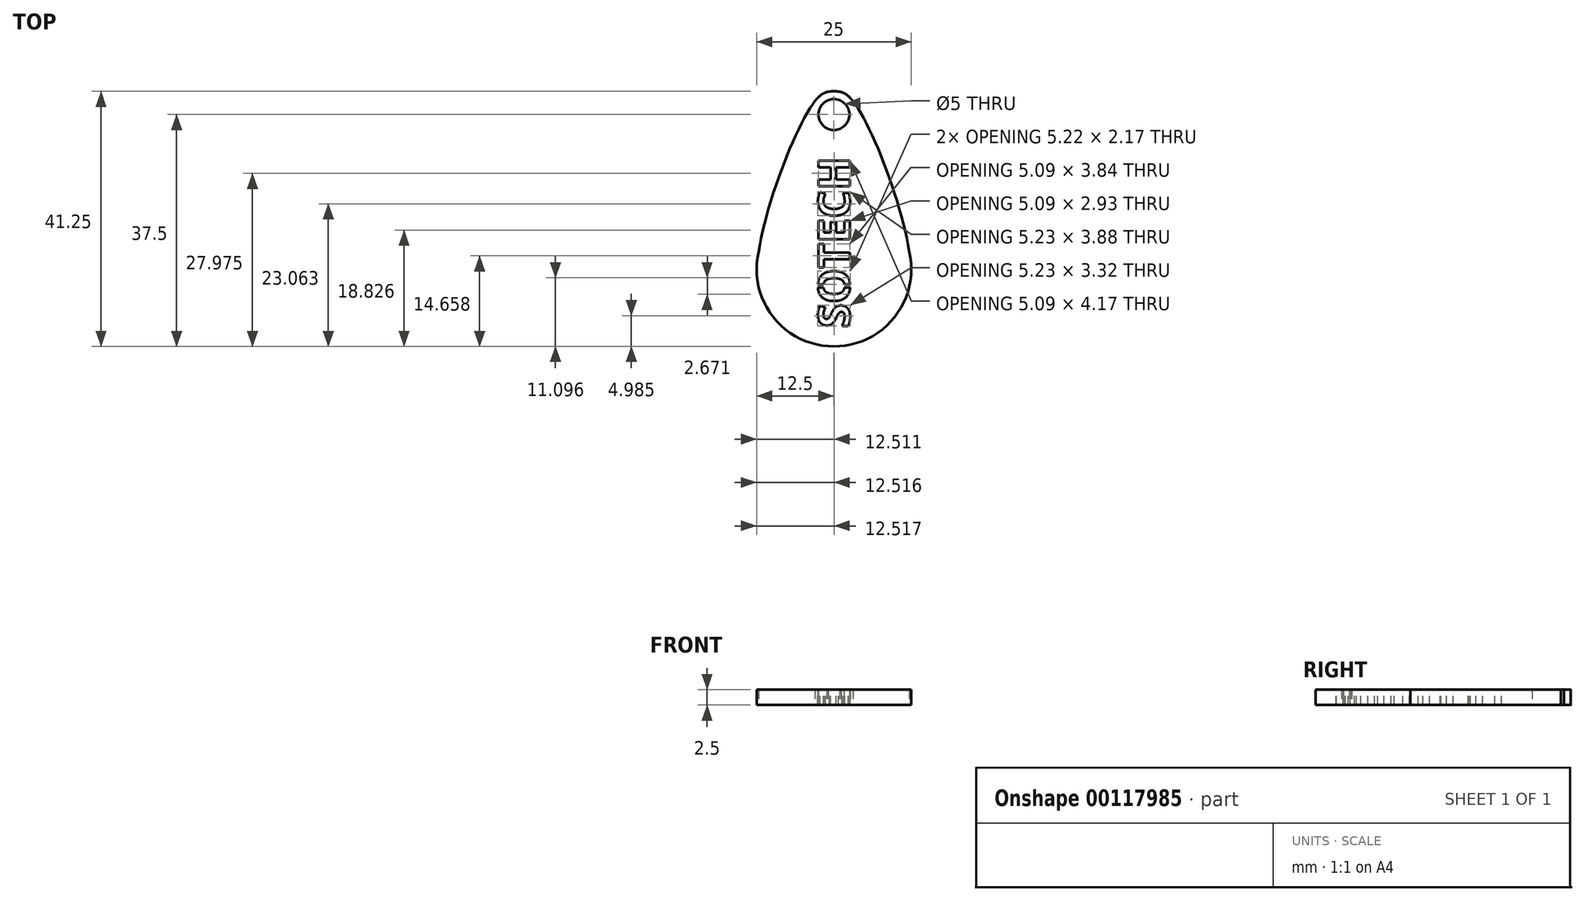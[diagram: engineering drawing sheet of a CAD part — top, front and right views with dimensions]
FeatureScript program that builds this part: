
annotation { "Feature Type Name" : "Feature", "Feature Type Description" : "" }
export const myFeature = defineFeature(function(context is Context, id is Id, definition is map)
    precondition{}
    {
        {
            var Q0;
            Q0=qCreatedBy(makeId("Top.planeOp"),FACE);
            var sketch = newSketch(context, id + "F0", { "sketchPlane" : qUnion([Q0])});
            skCircle(sketch, "E0", {"center": v(0, 0) * mm, "radius": 12.5 * mm});
            skLineSegment(sketch, "E1", {"start": v(0, 0) * mm, "end": v(0, 25) * mm, "construction": true});
            skCircle(sketch, "E2", {"center": v(0, 25) * mm, "radius": 3.75 * mm});
            skPoint(sketch, "E3", {"position": v(-8.84, -8.84) * mm});
            skPoint(sketch, "E4", {"position": v(-12.5, 0) * mm});
            skPoint(sketch, "E5", {"position": v(12.5, 0) * mm});
            skLineSegment(sketch, "E6", {"start": v(-12.5, 0) * mm, "end": v(0, 0) * mm, "construction": true});
            skLineSegment(sketch, "E7", {"start": v(0, 0) * mm, "end": v(12.5, 0) * mm, "construction": true});
            skLineSegment(sketch, "E8", {"start": v(0, 0) * mm, "end": v(-8.84, -8.84) * mm, "construction": true});
            skLineSegment(sketch, "E9", {"start": v(-8.84, -8.84) * mm, "end": v(8.84, -8.84) * mm, "construction": true});
            skLineSegment(sketch, "E10", {"start": v(8.84, -8.84) * mm, "end": v(0, 0) * mm, "construction": true});
            skPoint(sketch, "E11", {"position": v(-2.65, 27.65) * mm});
            skLineSegment(sketch, "E12", {"start": v(0, 25) * mm, "end": v(-3.75, 25) * mm, "construction": true});
            skLineSegment(sketch, "E13", {"start": v(0, 25) * mm, "end": v(-2.65, 27.65) * mm, "construction": true});
            skLineSegment(sketch, "E14", {"start": v(-2.65, 27.65) * mm, "end": v(2.65, 27.65) * mm, "construction": true});
            skLineSegment(sketch, "E15", {"start": v(2.65, 27.65) * mm, "end": v(0, 25) * mm, "construction": true});
            skPoint(sketch, "E16", {"position": v(0, 28.75) * mm});
            skPoint(sketch, "E17", {"position": v(0, -12.5) * mm});
            skPoint(sketch, "E17.positionSnap0", {"position": v(0, -8.84) * mm});
            skFitSpline(sketch, "E18", {"points": [v(0, 28.75) * mm, v(-2.65, 27.65) * mm, v(-12.5, 0) * mm, v(-8.84, -8.84) * mm, v(0, -12.5) * mm, v(8.84, -8.84) * mm, v(12.5, 0) * mm, v(2.65, 27.65) * mm, v(0, 28.75) * mm]});
            skCircle(sketch, "E19", {"center": v(0, 25) * mm, "radius": 2.5 * mm});
            skSolve(sketch);
        }
        {
            var Q0;
            {var subQ0=sQuery(id+"F0.wireOp",EDGE,"E18");var subQ1=sQuery(id+"F0.wireOp",EDGE,"E0");var subQ2=makeQuery(id+"F0.imprint","INTERSECT",VERTEX,{"disambiguationData":[OD(0.0)],"derivedFrom":[subQ1,subQ0]});Q0=makeQuery(id+"F0.imprint","IMPRINT",FACE,{"disambiguationData":[TD([[makeQuery(id+"F0.imprint","IMPRINT",EDGE,{"disambiguationData":[TD([[subQ2,1.0]])],"derivedFrom":subQ1}),1.0]])]});}
            var Q1;
            {var subQ0=sQuery(id+"F0.wireOp",EDGE,"E18");var subQ1=sQuery(id+"F0.wireOp",EDGE,"E0");var subQ2=makeQuery(id+"F0.imprint","INTERSECT",VERTEX,{"disambiguationData":[OD(2.0)],"derivedFrom":[subQ1,subQ0]});Q1=makeQuery(id+"F0.imprint","IMPRINT",FACE,{"disambiguationData":[TD([[makeQuery(id+"F0.imprint","IMPRINT",EDGE,{"disambiguationData":[TD([[subQ2,-1.0]])],"derivedFrom":subQ1}),1.0]])]});}
            var Q2;
            {var subQ0=sQuery(id+"F0.wireOp",EDGE,"E18");var subQ1=sQuery(id+"F0.wireOp",EDGE,"E2");var subQ2=makeQuery(id+"F0.imprint","INTERSECT",VERTEX,{"disambiguationData":[OD(0.0)],"derivedFrom":[subQ1,subQ0]});Q2=makeQuery(id+"F0.imprint","IMPRINT",FACE,{"disambiguationData":[TD([[makeQuery(id+"F0.imprint","IMPRINT",EDGE,{"disambiguationData":[TD([[subQ2,1.0]])],"derivedFrom":subQ1}),1.0]])]});}
            var Q3;
            {var subQ0=sQuery(id+"F0.wireOp",EDGE,"E18");var subQ1=sQuery(id+"F0.wireOp",EDGE,"E2");var subQ2=makeQuery(id+"F0.imprint","INTERSECT",VERTEX,{"disambiguationData":[OD(0.0)],"derivedFrom":[subQ1,subQ0]});Q3=makeQuery(id+"F0.imprint","IMPRINT",FACE,{"disambiguationData":[TD([[makeQuery(id+"F0.imprint","IMPRINT",EDGE,{"disambiguationData":[TD([[subQ2,-1.0]])],"derivedFrom":subQ1}),-1.0]])]});}
            var Q4;
            {var subQ0=sQuery(id+"F0.wireOp",EDGE,"E18");var subQ1=sQuery(id+"F0.wireOp",EDGE,"E2");var subQ2=makeQuery(id+"F0.imprint","INTERSECT",VERTEX,{"disambiguationData":[OD(2.0)],"derivedFrom":[subQ1,subQ0]});Q4=makeQuery(id+"F0.imprint","IMPRINT",FACE,{"disambiguationData":[TD([[makeQuery(id+"F0.imprint","IMPRINT",EDGE,{"disambiguationData":[TD([[subQ2,-1.0]])],"derivedFrom":subQ1}),-1.0]])]});}
            var Q5;
            {var subQ0=sQuery(id+"F0.wireOp",EDGE,"E18");var subQ1=sQuery(id+"F0.wireOp",EDGE,"E2");var subQ2=makeQuery(id+"F0.imprint","INTERSECT",VERTEX,{"disambiguationData":[OD(3.0)],"derivedFrom":[subQ1,subQ0]});Q5=makeQuery(id+"F0.imprint","IMPRINT",FACE,{"disambiguationData":[TD([[makeQuery(id+"F0.imprint","IMPRINT",EDGE,{"disambiguationData":[TD([[subQ2,-1.0]])],"derivedFrom":subQ1}),1.0]])]});}
            var Q6;
            {var subQ0=sQuery(id+"F0.wireOp",EDGE,"E18");var subQ1=sQuery(id+"F0.wireOp",EDGE,"E0");var subQ2=makeQuery(id+"F0.imprint","INTERSECT",VERTEX,{"disambiguationData":[OD(0.0)],"derivedFrom":[subQ1,subQ0]});Q6=makeQuery(id+"F0.imprint","IMPRINT",FACE,{"disambiguationData":[TD([[makeQuery(id+"F0.imprint","IMPRINT",EDGE,{"disambiguationData":[TD([[subQ2,-1.0]])],"derivedFrom":subQ1}),-1.0]])]});}
            var Q7;
            Q7=makeQuery(id+"F0.imprint","IMPRINT",FACE,{"disambiguationData":[TD([[makeQuery(id+"F0.imprint","IMPRINT",EDGE,{"derivedFrom":sQuery(id+"F0.wireOp",EDGE,"E19")}),-1.0]])]});
            var Q8;
            {var subQ0=sQuery(id+"F0.wireOp",EDGE,"E18");var subQ1=sQuery(id+"F0.wireOp",EDGE,"E0");var subQ8=makeQuery(id+"F0.imprint","INTERSECT",VERTEX,{"disambiguationData":[OD(0.0)],"derivedFrom":[subQ1,subQ0]});Q8=makeQuery(id+"F0.imprint","IMPRINT",FACE,{"disambiguationData":[TD([[makeQuery(id+"F0.imprint","IMPRINT",EDGE,{"disambiguationData":[TD([[subQ8,-1.0]])],"derivedFrom":subQ1}),1.0]])]});}
            var Q9;
            {var subQ0=sQuery(id+"F0.wireOp",EDGE,"E18");var subQ1=sQuery(id+"F0.wireOp",EDGE,"E0");var subQ2=makeQuery(id+"F0.imprint","INTERSECT",VERTEX,{"disambiguationData":[OD(4.0)],"derivedFrom":[subQ1,subQ0]});Q9=makeQuery(id+"F0.imprint","IMPRINT",FACE,{"disambiguationData":[TD([[makeQuery(id+"F0.imprint","IMPRINT",EDGE,{"disambiguationData":[TD([[subQ2,-1.0]])],"derivedFrom":subQ1}),1.0]])]});}
            var Q10;
            {var subQ0=sQuery(id+"F0.wireOp",EDGE,"E18");var subQ1=sQuery(id+"F0.wireOp",EDGE,"E0");var subQ2=makeQuery(id+"F0.imprint","INTERSECT",VERTEX,{"disambiguationData":[OD(5.0)],"derivedFrom":[subQ1,subQ0]});Q10=makeQuery(id+"F0.imprint","IMPRINT",FACE,{"disambiguationData":[TD([[makeQuery(id+"F0.imprint","IMPRINT",EDGE,{"disambiguationData":[TD([[subQ2,-1.0]])],"derivedFrom":subQ1}),1.0]])]});}
            extrude(context, id + "F1", {"entities" : qUnion([Q0, Q1, Q2, Q3, Q4, Q5, Q6, Q7, Q8, Q9, Q10]), "depth" : 2.5 * mm});
        }
        {
            var Q0;
            Q0=makeQuery(id+"F1.opExtrude","CAP_FACE",FACE,{"disambiguationData":[OSD([sQuery(id+"F0.wireOp",EDGE,"E0"),sQuery(id+"F0.wireOp",EDGE,"E2"),sQuery(id+"F0.wireOp",EDGE,"E18"),sQuery(id+"F0.wireOp",EDGE,"E19")])],"isStart":false});
            var sketch = newSketch(context, id + "F2", { "sketchPlane" : qUnion([Q0])});
            skText(sketch, "E20", { "text": "SOTECH", "fontName": "OpenSans-Bold.ttf"});
            skLineSegment(sketch, "E21", {"start": v(0, 0) * mm, "end": v(0, 28.75) * mm, "construction": true});
            skPoint(sketch, "E22", {"position": v(0, -9.5) * mm});
            skLineSegment(sketch, "E23", {"start": v(0, 0) * mm, "end": v(0, -12.5) * mm, "construction": true});
            const initialGuessF2  = {"E20": [0.00256, -0.0095, 0, 1, 0.00513]};
            skSetInitialGuess(sketch, initialGuessF2);
            skSolve(sketch);
        }
        {
            var Q0;
            Q0=makeQuery(id+"F2.imprint","IMPRINT",FACE,{"disambiguationData":[TD([[makeQuery(id+"F2.imprint","IMPRINT",EDGE,{"derivedFrom":sQuery(id+"F2.wireOp",EDGE,"E20.sketch_text.stroke-77")}),-1.0]])]});
            var Q1;
            Q1=makeQuery(id+"F2.imprint","IMPRINT",FACE,{"disambiguationData":[TD([[makeQuery(id+"F2.imprint","IMPRINT",EDGE,{"derivedFrom":sQuery(id+"F2.wireOp",EDGE,"E20.sketch_text.stroke-0")}),-1.0]])]});
            var Q2;
            Q2=makeQuery(id+"F2.imprint","IMPRINT",FACE,{"disambiguationData":[TD([[makeQuery(id+"F2.imprint","IMPRINT",EDGE,{"derivedFrom":sQuery(id+"F2.wireOp",EDGE,"E20.sketch_text.stroke-28")}),-1.0]])]});
            var Q3;
            Q3=makeQuery(id+"F2.imprint","IMPRINT",FACE,{"disambiguationData":[TD([[makeQuery(id+"F2.imprint","IMPRINT",EDGE,{"derivedFrom":sQuery(id+"F2.wireOp",EDGE,"E20.sketch_text.stroke-42")}),-1.0]])]});
            var Q4;
            Q4=makeQuery(id+"F2.imprint","IMPRINT",FACE,{"disambiguationData":[TD([[makeQuery(id+"F2.imprint","IMPRINT",EDGE,{"derivedFrom":sQuery(id+"F2.wireOp",EDGE,"E20.sketch_text.stroke-50")}),-1.0]])]});
            var Q5;
            Q5=makeQuery(id+"F2.imprint","IMPRINT",FACE,{"disambiguationData":[TD([[makeQuery(id+"F2.imprint","IMPRINT",EDGE,{"derivedFrom":sQuery(id+"F2.wireOp",EDGE,"E20.sketch_text.stroke-62")}),-1.0]])]});
            extrude(context, id + "F3", {"entities" : qUnion([Q0, Q1, Q2, Q3, Q4, Q5]), "operationType" : NewBodyOperationType.REMOVE, "oppositeDirection" : true, "depth" : 25 * mm});
        }
        {
            var Q0;
            {var subQ0=sQuery(id+"F0.wireOp",EDGE,"E19");var subQ1=sQuery(id+"F0.wireOp",EDGE,"E18");var subQ2=sQuery(id+"F0.wireOp",EDGE,"E0");var subQ3=sQuery(id+"F0.wireOp",EDGE,"E2");Q0=makeQuery(id+"F3.boolean.opBoolean","SPLIT",FACE,{"disambiguationData":[TD([makeQuery(id+"F1.opExtrude","SWEPT_FACE",FACE,{"disambiguationData":[OSD([subQ2])]})])],"derivedFrom":makeQuery(id+"F1.opExtrude","CAP_FACE",FACE,{"disambiguationData":[OSD([subQ2,subQ3,subQ1,subQ0])],"isStart":false})});}
            var sketch = newSketch(context, id + "F4", { "sketchPlane" : qUnion([Q0])});
            skLineSegment(sketch, "E24.bottom", {"start": v(3.34, -2.49) * mm, "end": v(-3.34, -2.49) * mm});
            skLineSegment(sketch, "E24.top", {"start": v(3.34, -2.99) * mm, "end": v(-3.34, -2.99) * mm});
            skLineSegment(sketch, "E24.left", {"start": v(3.34, -2.49) * mm, "end": v(3.34, -2.99) * mm});
            skLineSegment(sketch, "E24.right", {"start": v(-3.34, -2.49) * mm, "end": v(-3.34, -2.99) * mm});
            skPoint(sketch, "E24.middle", {"position": v(0, -2.74) * mm});
            skSolve(sketch);
        }
        {
            var Q0;
            {var subQ5=sQuery(id+"F4.wireOp",EDGE,"E24.left");Q0=makeQuery(id+"F4.imprint","IMPRINT",FACE,{"disambiguationData":[TD([[makeQuery(id+"F4.imprint","IMPRINT",EDGE,{"derivedFrom":subQ5}),-1.0]])]});}
            var Q1;
            {var subQ5=sQuery(id+"F4.wireOp",EDGE,"E24.right");Q1=makeQuery(id+"F4.imprint","IMPRINT",FACE,{"disambiguationData":[TD([[makeQuery(id+"F4.imprint","IMPRINT",EDGE,{"derivedFrom":subQ5}),1.0]])]});}
            var Q2;
            {var subQ1=makeQuery(id+"F3.boolean.opBoolean","COPY",EDGE,{"derivedFrom":makeQuery(id+"F3.opExtrude","CAP_EDGE",EDGE,{"disambiguationData":[OSD([sQuery(id+"F2.wireOp",EDGE,"E20.sketch_text.stroke-29")])],"isStart":true})});var subQ3=sQuery(id+"F4.wireOp",EDGE,"E24.bottom");var subQ4=makeQuery(id+"F4.imprint","INTERSECT",VERTEX,{"derivedFrom":[subQ1,subQ3]});Q2=makeQuery(id+"F4.imprint","IMPRINT",FACE,{"disambiguationData":[TD([[makeQuery(id+"F4.imprint","IMPRINT",EDGE,{"disambiguationData":[TD([[subQ4,-1.0]])],"derivedFrom":subQ3}),1.0]])]});}
            var Q3;
            {var subQ0=sQuery(id+"F0.wireOp",EDGE,"E19");var subQ1=sQuery(id+"F0.wireOp",EDGE,"E18");var subQ2=sQuery(id+"F0.wireOp",EDGE,"E0");var subQ3=sQuery(id+"F0.wireOp",EDGE,"E2");Q3=makeQuery(id+"F3.boolean.opBoolean","SPLIT",FACE,{"disambiguationData":[TD([makeQuery(id+"F1.opExtrude","SWEPT_FACE",FACE,{"disambiguationData":[OSD([subQ2])]})])],"derivedFrom":makeQuery(id+"F1.opExtrude","CAP_FACE",FACE,{"disambiguationData":[OSD([subQ2,subQ3,subQ1,subQ0])],"isStart":true})});}
            extrude(context, id + "F5", {"entities" : qUnion([Q0, Q1, Q2]), "operationType" : NewBodyOperationType.ADD, "endBound" : BoundingType.UP_TO_SURFACE, "oppositeDirection" : true, "endBoundEntityFace" : qUnion([Q3]), "depth" : 25 * mm});
        }
    });
